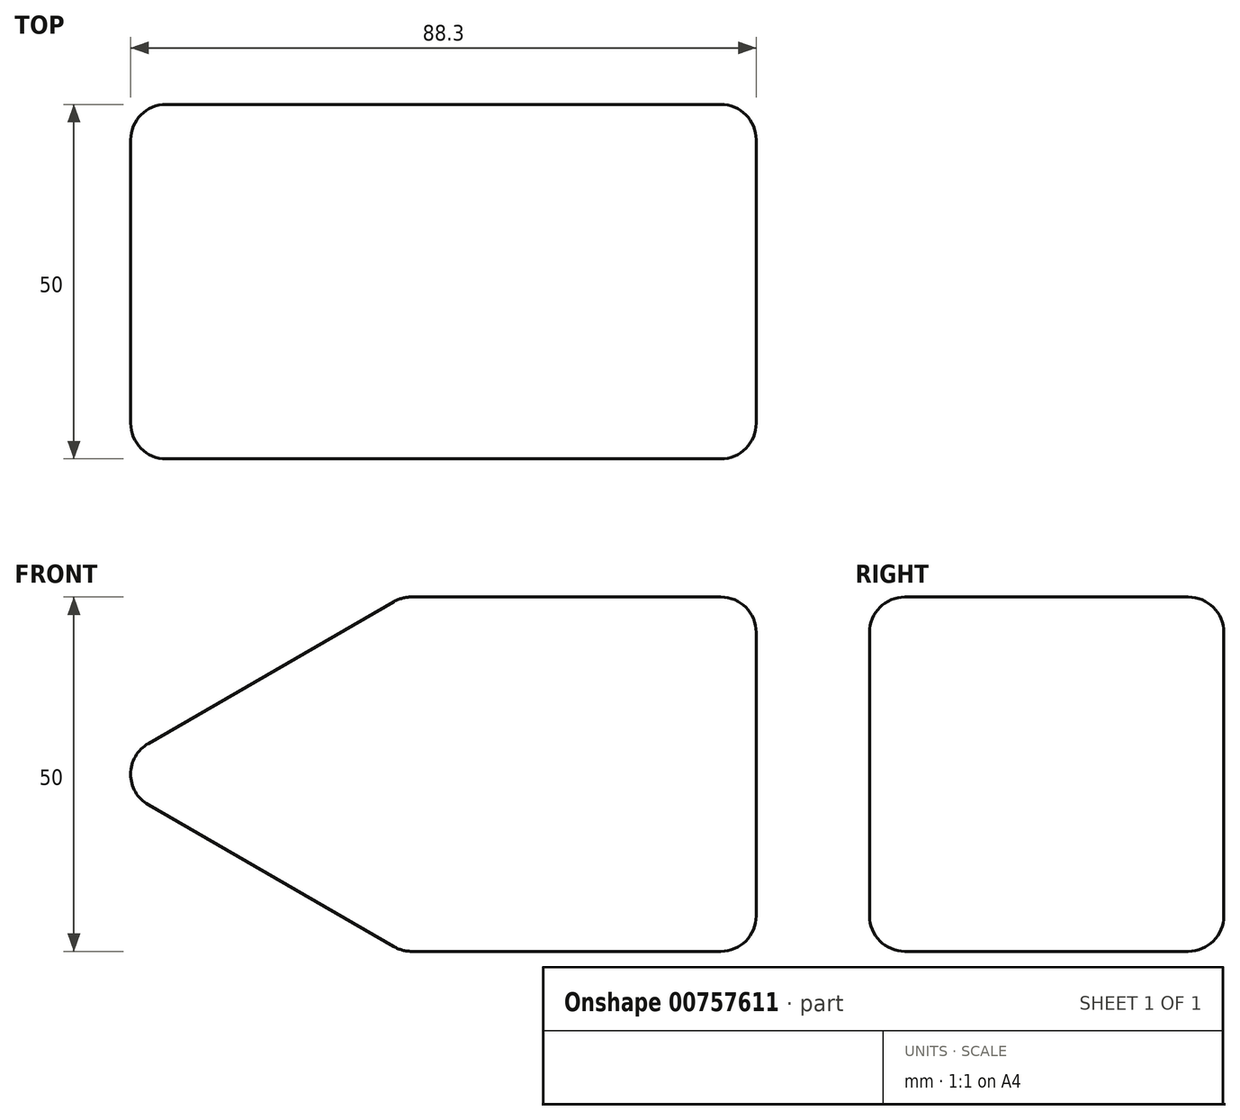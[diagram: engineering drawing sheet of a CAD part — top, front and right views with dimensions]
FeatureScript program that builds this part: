
annotation { "Feature Type Name" : "Feature", "Feature Type Description" : "" }
export const myFeature = defineFeature(function(context is Context, id is Id, definition is map)
    precondition{}
    {
        {
            var Q0;
            Q0=qCreatedBy(makeId("Front.planeOp"),FACE);
            var sketch = newSketch(context, id + "F0", { "sketchPlane" : qUnion([Q0])});
            skLineSegment(sketch, "E0", {"start": v(0, 0) * mm, "end": v(50, 0) * mm});
            skLineSegment(sketch, "E1", {"start": v(50, 0) * mm, "end": v(50, -50) * mm});
            skLineSegment(sketch, "E2", {"start": v(50, -50) * mm, "end": v(0, -50) * mm});
            skLineSegment(sketch, "E3", {"start": v(0, -50) * mm, "end": v(-43.3, -25) * mm});
            skLineSegment(sketch, "E4", {"start": v(-43.3, -25) * mm, "end": v(0, 0) * mm});
            skLineSegment(sketch, "E5", {"start": v(50, -25) * mm, "end": v(-43.3, -25) * mm});
            skSolve(sketch);
        }
        {
            var Q0;
            {var subQ0=sQuery(id+"F0.wireOp",EDGE,"E2");Q0=makeQuery(id+"F0.imprint","IMPRINT",FACE,{"disambiguationData":[TD([[makeQuery(id+"F0.imprint","IMPRINT",EDGE,{"derivedFrom":subQ0}),-1.0]])]});}
            var Q1;
            {var subQ0=sQuery(id+"F0.wireOp",EDGE,"E0");Q1=makeQuery(id+"F0.imprint","IMPRINT",FACE,{"disambiguationData":[TD([[makeQuery(id+"F0.imprint","IMPRINT",EDGE,{"derivedFrom":subQ0}),-1.0]])]});}
            extrude(context, id + "F1", {"entities" : qUnion([Q0, Q1]), "depth" : 50 * mm, "offsetDistance" : 25 * mm});
        }
        {
            var Q0;
            Q0=makeQuery(id+"F1.opExtrude","CAP_EDGE",EDGE,{"disambiguationData":[OSD([sQuery(id+"F0.wireOp",EDGE,"E4")])],"isStart":false});
            var Q1;
            Q1=makeQuery(id+"F1.opExtrude","CAP_EDGE",EDGE,{"disambiguationData":[OSD([sQuery(id+"F0.wireOp",EDGE,"E3")])],"isStart":false});
            var Q2;
            Q2=makeQuery(id+"F1.opExtrude","SWEPT_EDGE",EDGE,{"disambiguationData":[OSD([sQuery(id+"F0.wireOp",EDGE,"E2"),sQuery(id+"F0.wireOp",EDGE,"E3")])]});
            var Q3;
            Q3=makeQuery(id+"F1.opExtrude","CAP_EDGE",EDGE,{"disambiguationData":[OSD([sQuery(id+"F0.wireOp",EDGE,"E3")])],"isStart":true});
            var Q4;
            Q4=makeQuery(id+"F1.opExtrude","SWEPT_EDGE",EDGE,{"disambiguationData":[OSD([sQuery(id+"F0.wireOp",EDGE,"E3"),sQuery(id+"F0.wireOp",EDGE,"E4"),sQuery(id+"F0.wireOp",EDGE,"E5")])]});
            var Q5;
            Q5=makeQuery(id+"F1.opExtrude","CAP_EDGE",EDGE,{"disambiguationData":[OSD([sQuery(id+"F0.wireOp",EDGE,"E4")])],"isStart":true});
            var Q6;
            Q6=makeQuery(id+"F1.opExtrude","SWEPT_EDGE",EDGE,{"disambiguationData":[OSD([sQuery(id+"F0.wireOp",EDGE,"E0"),sQuery(id+"F0.wireOp",EDGE,"E4")])]});
            var Q7;
            Q7=makeQuery(id+"F1.opExtrude","CAP_EDGE",EDGE,{"disambiguationData":[OSD([sQuery(id+"F0.wireOp",EDGE,"E2")])],"isStart":true});
            var Q8;
            Q8=makeQuery(id+"F1.opExtrude","CAP_EDGE",EDGE,{"disambiguationData":[OSD([sQuery(id+"F0.wireOp",EDGE,"E0")])],"isStart":true});
            var Q9;
            Q9=makeQuery(id+"F1.opExtrude","CAP_EDGE",EDGE,{"disambiguationData":[OSD([sQuery(id+"F0.wireOp",EDGE,"E0")])],"isStart":false});
            var Q10;
            Q10=makeQuery(id+"F1.opExtrude","CAP_EDGE",EDGE,{"disambiguationData":[OSD([sQuery(id+"F0.wireOp",EDGE,"E2")])],"isStart":false});
            var Q11;
            Q11=makeQuery(id+"F1.opExtrude","SWEPT_EDGE",EDGE,{"disambiguationData":[OSD([sQuery(id+"F0.wireOp",EDGE,"E1"),sQuery(id+"F0.wireOp",EDGE,"E2")])]});
            var Q12;
            Q12=makeQuery(id+"F1.opExtrude","CAP_EDGE",EDGE,{"disambiguationData":[OSD([sQuery(id+"F0.wireOp",EDGE,"E1")])],"isStart":false});
            var Q13;
            Q13=makeQuery(id+"F1.opExtrude","SWEPT_EDGE",EDGE,{"disambiguationData":[OSD([sQuery(id+"F0.wireOp",EDGE,"E0"),sQuery(id+"F0.wireOp",EDGE,"E1")])]});
            var Q14;
            Q14=makeQuery(id+"F1.opExtrude","CAP_EDGE",EDGE,{"disambiguationData":[OSD([sQuery(id+"F0.wireOp",EDGE,"E1")])],"isStart":true});
            fillet(context, id + "F2", {"entities" : qUnion([Q0, Q1, Q2, Q3, Q4, Q5, Q6, Q7, Q8, Q9, Q10, Q11, Q12, Q13, Q14]), "radius" : 5 * mm, "tangentPropagation" : true, "allowEdgeOverflow" : false});
        }
    });
